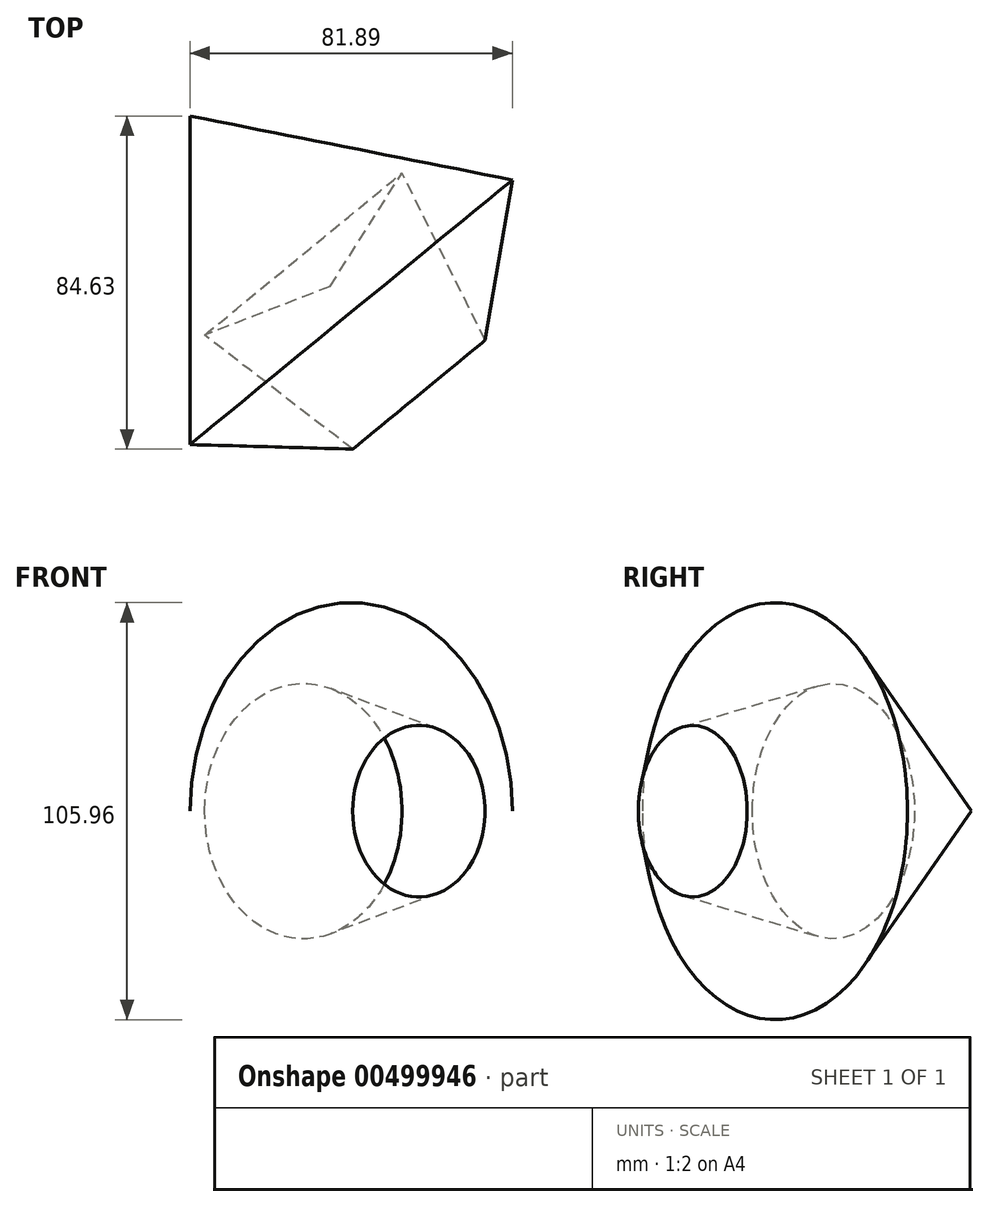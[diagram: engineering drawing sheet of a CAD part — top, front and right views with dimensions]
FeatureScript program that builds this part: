
annotation { "Feature Type Name" : "Feature", "Feature Type Description" : "" }
export const myFeature = defineFeature(function(context is Context, id is Id, definition is map)
    precondition{}
    {
        {
            var Q0;
            Q0=qCreatedBy(makeId("Top.planeOp"),FACE);
            var sketch = newSketch(context, id + "F0", { "sketchPlane" : qUnion([Q0])});
            skLineSegment(sketch, "E0", {"start": v(-55.08, 36.86) * mm, "end": v(-55.08, -46.62) * mm});
            skLineSegment(sketch, "E1", {"start": v(-55.08, 36.86) * mm, "end": v(-19.5, -6.45) * mm});
            skLineSegment(sketch, "E2", {"start": v(-19.5, -6.45) * mm, "end": v(-51.35, -18.8) * mm});
            skLineSegment(sketch, "E3", {"start": v(-51.35, -18.8) * mm, "end": v(-13.77, -47.77) * mm});
            skLineSegment(sketch, "E4", {"start": v(-13.77, -47.77) * mm, "end": v(-55.08, -46.62) * mm});
            skSolve(sketch);
        }
        {
            var Q0;
            Q0=makeQuery(id+"F0.imprint","IMPRINT",FACE,{"disambiguationData":[TD([[makeQuery(id+"F0.imprint","IMPRINT",EDGE,{"derivedFrom":sQuery(id+"F0.wireOp",EDGE,"E0")}),1.0]])]});
            var Q1;
            Q1=sQuery(id+"F0.wireOp",EDGE,"E1");
            revolve(context, id + "F1", {"entities" : qUnion([Q0]), "axis" : qUnion([Q1]), "revolveType" : RevolveType.FULL});
        }
    });
